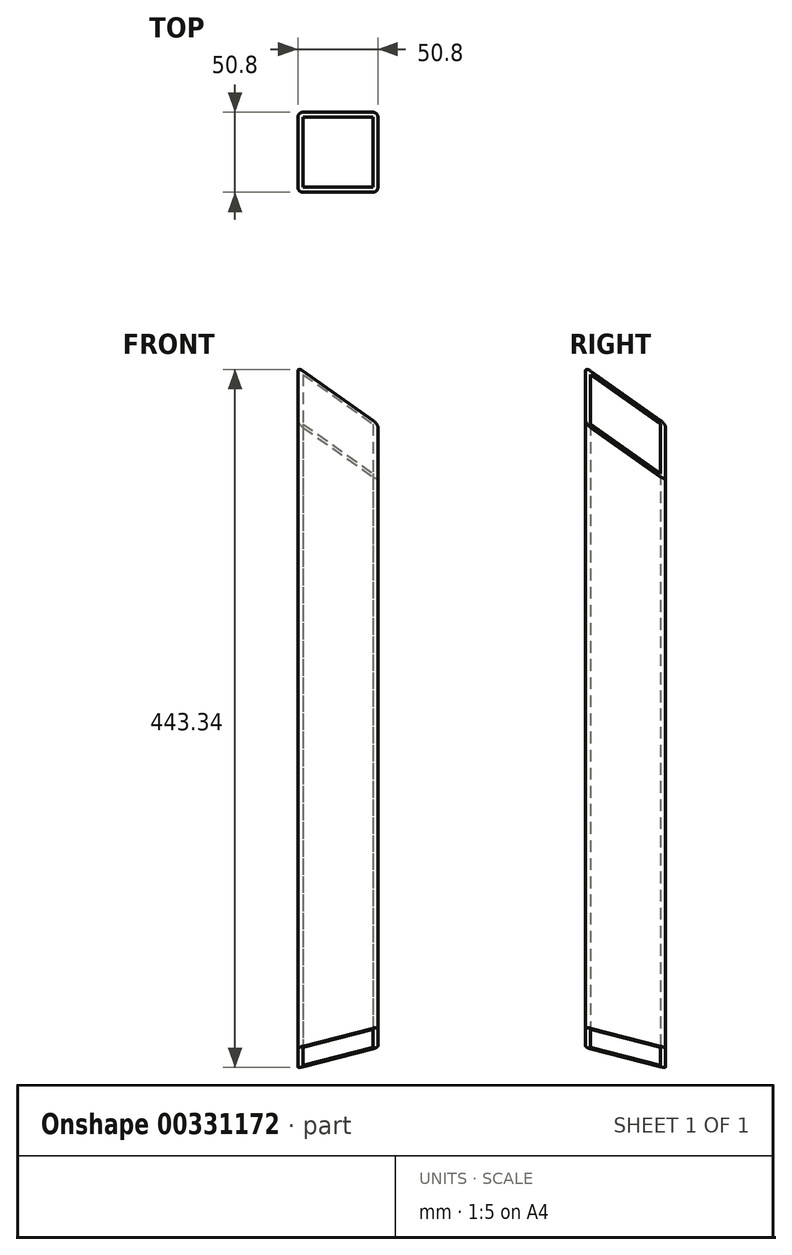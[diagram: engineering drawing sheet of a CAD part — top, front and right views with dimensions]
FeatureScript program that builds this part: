
annotation { "Feature Type Name" : "Feature", "Feature Type Description" : "" }
export const myFeature = defineFeature(function(context is Context, id is Id, definition is map)
    precondition{}
    {
        {
            var Q0;
            Q0=qCreatedBy(makeId("Top.planeOp"),FACE);
            var sketch = newSketch(context, id + "F0", { "sketchPlane" : qUnion([Q0])});
            skLineSegment(sketch, "E0.bottom", {"start": v(22.23, 25.4) * mm, "end": v(-22.23, 25.4) * mm});
            skLineSegment(sketch, "E0.top", {"start": v(22.22, -25.4) * mm, "end": v(-22.22, -25.4) * mm});
            skLineSegment(sketch, "E0.left", {"start": v(25.4, 22.23) * mm, "end": v(25.4, -22.22) * mm});
            skLineSegment(sketch, "E0.right", {"start": v(-25.4, 22.23) * mm, "end": v(-25.4, -22.22) * mm});
            skPoint(sketch, "E0.middle", {"position": v(0, 0) * mm});
            skPoint(sketch, "E1.visualSharp", {"position": v(-25.4, 25.4) * mm});
            skArc(sketch, "E1.filletArc", {"start": v(-22.23, 25.4) * mm, "mid": v(-24.47, 24.47) * mm, "end": v(-25.4, 22.23) * mm});
            skPoint(sketch, "E2.visualSharp", {"position": v(25.4, 25.4) * mm});
            skArc(sketch, "E2.filletArc", {"start": v(25.4, 22.23) * mm, "mid": v(24.47, 24.47) * mm, "end": v(22.23, 25.4) * mm});
            skPoint(sketch, "E3.visualSharp", {"position": v(-25.4, -25.4) * mm});
            skArc(sketch, "E3.filletArc", {"start": v(-25.4, -22.22) * mm, "mid": v(-24.47, -24.47) * mm, "end": v(-22.22, -25.4) * mm});
            skPoint(sketch, "E4.visualSharp", {"position": v(25.4, -25.4) * mm});
            skArc(sketch, "E4.filletArc", {"start": v(22.22, -25.4) * mm, "mid": v(24.47, -24.47) * mm, "end": v(25.4, -22.22) * mm});
            skLineSegment(sketch, "E5.0", {"start": v(22.23, 22.23) * mm, "end": v(-22.23, 22.23) * mm});
            skLineSegment(sketch, "E5.1", {"start": v(22.23, 22.23) * mm, "end": v(22.23, -22.23) * mm});
            skLineSegment(sketch, "E5.2", {"start": v(22.23, -22.23) * mm, "end": v(-22.23, -22.23) * mm});
            skLineSegment(sketch, "E5.3", {"start": v(-22.23, 22.23) * mm, "end": v(-22.23, -22.23) * mm});
            skLineSegment(sketch, "E6", {"start": v(22.22, -22.22) * mm, "end": v(-22.23, 22.23) * mm, "construction": true});
            skSolve(sketch);
        }
        {
            var Q0;
            Q0 = qSketchRegion(id + "F0", true);
            extrude(context, id + "F1", {"entities" : qUnion([Q0]), "depth" : 457.2 * mm});
        }
        {
            var Q0;
            Q0=makeQuery(id+"F1.opExtrude","CAP_FACE",FACE,{"disambiguationData":[OSD([sQuery(id+"F0.wireOp",EDGE,"E0.bottom"),sQuery(id+"F0.wireOp",EDGE,"E0.top"),sQuery(id+"F0.wireOp",EDGE,"E0.left"),sQuery(id+"F0.wireOp",EDGE,"E0.right"),sQuery(id+"F0.wireOp",EDGE,"E1.filletArc"),sQuery(id+"F0.wireOp",EDGE,"E2.filletArc"),sQuery(id+"F0.wireOp",EDGE,"E3.filletArc"),sQuery(id+"F0.wireOp",EDGE,"E4.filletArc"),sQuery(id+"F0.wireOp",EDGE,"E5.0"),sQuery(id+"F0.wireOp",EDGE,"E5.1"),sQuery(id+"F0.wireOp",EDGE,"E5.2"),sQuery(id+"F0.wireOp",EDGE,"E5.3")])],"isStart":false});
            var sketch = newSketch(context, id + "F2", { "sketchPlane" : qUnion([Q0])});
            skLineSegment(sketch, "E7", {"start": v(-22.22, 22.22) * mm, "end": v(22.22, -22.22) * mm});
            skSolve(sketch);
        }
        {
            var Q0;
            Q0=sQuery(id+"F2.wireOp",EDGE,"E7");
            cPlane(context, id + "F3", {"entities" : qUnion([Q0]), "cplaneType" : CPlaneType.LINE_ANGLE, "offset" : 25.4 * mm, "angle" : 45 * degree, "oppositeDirection" : true, "width" : 152.4 * mm, "height" : 152.4 * mm});
        }
        {
            var Q0;
            Q0=qCreatedBy(id+"F3.planeOp",FACE);
            var sketch = newSketch(context, id + "F4", { "sketchPlane" : qUnion([Q0])});
            skPoint(sketch, "E8", {"position": v(-186.65, 264.08) * mm});
            skLineSegment(sketch, "E9", {"start": v(-186.65, 264.08) * mm, "end": v(-262.85, 340.28) * mm});
            skLineSegment(sketch, "E10", {"start": v(-262.85, 340.28) * mm, "end": v(-110.45, 187.88) * mm});
            skLineSegment(sketch, "E11", {"start": v(-110.45, 187.88) * mm, "end": v(-110.45, 340.28) * mm});
            skLineSegment(sketch, "E12", {"start": v(-110.45, 340.28) * mm, "end": v(-262.85, 340.28) * mm});
            skLineSegment(sketch, "E13", {"start": v(-262.85, 340.28) * mm, "end": v(-262.85, 187.88) * mm});
            skLineSegment(sketch, "E14", {"start": v(-262.85, 187.88) * mm, "end": v(-110.45, 187.88) * mm});
            skLineSegment(sketch, "E15", {"start": v(-110.45, 187.88) * mm, "end": v(-186.65, 264.08) * mm});
            skSolve(sketch);
        }
        {
            var Q0;
            Q0 = qSketchRegion(id + "F4", true);
            extrude(context, id + "F5", {"entities" : qUnion([Q0]), "operationType" : NewBodyOperationType.REMOVE, "oppositeDirection" : true, "depth" : 25.4 * mm, "hasSecondDirection" : true, "secondDirectionOppositeDirection" : false, "secondDirectionDepth" : 24.64 * mm});
        }
        {
            var Q0;
            Q0=makeQuery(id+"F1.opExtrude","CAP_FACE",FACE,{"disambiguationData":[OSD([sQuery(id+"F0.wireOp",EDGE,"E0.bottom"),sQuery(id+"F0.wireOp",EDGE,"E0.top"),sQuery(id+"F0.wireOp",EDGE,"E0.left"),sQuery(id+"F0.wireOp",EDGE,"E0.right"),sQuery(id+"F0.wireOp",EDGE,"E1.filletArc"),sQuery(id+"F0.wireOp",EDGE,"E2.filletArc"),sQuery(id+"F0.wireOp",EDGE,"E3.filletArc"),sQuery(id+"F0.wireOp",EDGE,"E4.filletArc"),sQuery(id+"F0.wireOp",EDGE,"E5.0"),sQuery(id+"F0.wireOp",EDGE,"E5.1"),sQuery(id+"F0.wireOp",EDGE,"E5.2"),sQuery(id+"F0.wireOp",EDGE,"E5.3")])],"isStart":true});
            var sketch = newSketch(context, id + "F6", { "sketchPlane" : qUnion([Q0])});
            skLineSegment(sketch, "E16", {"start": v(22.22, -22.22) * mm, "end": v(-22.22, 22.22) * mm});
            skSolve(sketch);
        }
        {
            var Q0;
            Q0=sQuery(id+"F6.wireOp",EDGE,"E16");
            cPlane(context, id + "F7", {"entities" : qUnion([Q0]), "cplaneType" : CPlaneType.LINE_ANGLE, "offset" : 25.4 * mm, "angle" : 20 * degree, "width" : 152.4 * mm, "height" : 152.4 * mm});
        }
        {
            var Q0;
            Q0=qCreatedBy(id+"F7.planeOp",FACE);
            var sketch = newSketch(context, id + "F8", { "sketchPlane" : qUnion([Q0])});
            skLineSegment(sketch, "E17.bottom", {"start": v(-76.2, -76.2) * mm, "end": v(76.2, -76.2) * mm});
            skLineSegment(sketch, "E17.top", {"start": v(-76.2, 76.2) * mm, "end": v(76.2, 76.2) * mm});
            skLineSegment(sketch, "E17.left", {"start": v(-76.2, -76.2) * mm, "end": v(-76.2, 76.2) * mm});
            skLineSegment(sketch, "E17.right", {"start": v(76.2, -76.2) * mm, "end": v(76.2, 76.2) * mm});
            skPoint(sketch, "E17.middle", {"position": v(0, 0) * mm});
            skSolve(sketch);
        }
        {
            var Q0;
            Q0 = qSketchRegion(id + "F8", true);
            extrude(context, id + "F9", {"entities" : qUnion([Q0]), "operationType" : NewBodyOperationType.REMOVE, "oppositeDirection" : true, "depth" : 24.64 * mm, "hasSecondDirection" : true, "secondDirectionOppositeDirection" : false, "secondDirectionDepth" : 25.4 * mm});
        }
    });
